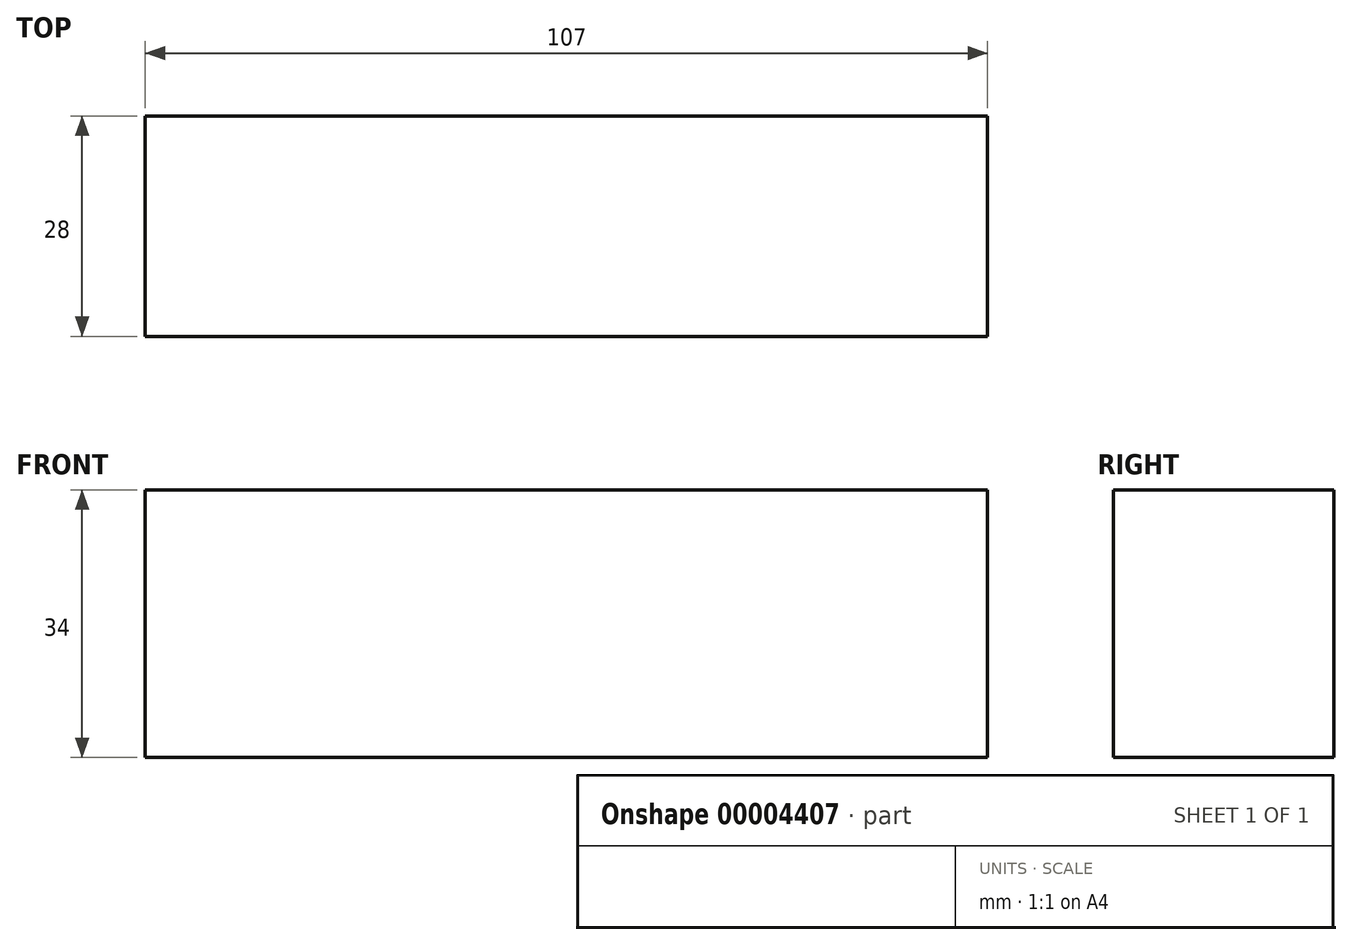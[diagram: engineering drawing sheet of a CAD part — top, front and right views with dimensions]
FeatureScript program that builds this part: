
annotation { "Feature Type Name" : "Feature", "Feature Type Description" : "" }
export const myFeature = defineFeature(function(context is Context, id is Id, definition is map)
    precondition{}
    {
        {
            var Q0;
            Q0=qCreatedBy(makeId("Front.planeOp"),FACE);
            var sketch = newSketch(context, id + "F0", { "sketchPlane" : qUnion([Q0])});
            skLineSegment(sketch, "E0.rect.bottom", {"start": v(53.5, 17) * mm, "end": v(-53.5, 17) * mm});
            skLineSegment(sketch, "E0.rect.top", {"start": v(53.5, -17) * mm, "end": v(-53.5, -17) * mm});
            skLineSegment(sketch, "E0.rect.left", {"start": v(53.5, 17) * mm, "end": v(53.5, -17) * mm});
            skLineSegment(sketch, "E0.rect.right", {"start": v(-53.5, 17) * mm, "end": v(-53.5, -17) * mm});
            skPoint(sketch, "E0.rect.middle", {"position": v(0, 0) * mm});
            skSolve(sketch);
        }
        {
            var Q0;
            Q0=makeQuery(id+"F0.imprint","IMPRINT",FACE,{"disambiguationData":[TD([[makeQuery(id+"F0.imprint","IMPRINT",EDGE,{"derivedFrom":sQuery(id+"F0.wireOp",EDGE,"E0.rect.bottom")}),1.0]])]});
            extrude(context, id + "F1", {"entities" : qUnion([Q0]), "depth" : 28 * mm});
        }
    });
